# Revit family: Grab Rail_Metlam_Straight_Horizontal
name_source: partatom
category: Specialty Equipment
revit_build: Autodesk Revit 2016 (Build: 20170117_1200(x64)
units: mm (PartAtom-declared; Revit-internal decimal feet)

## family parameters
Always vertical = Yes
Cut with Voids When Loaded = No
OmniClass Number = 23.40.20.21.47
OmniClass Title = Bath Grab Bars
Part Type = Normal
Room Calculation Point = Yes
Round Connector Dimension = Use Diameter
Shared = No
Work Plane-Based = No

## types (10) — shared parameters
Depth = 90 mm  [stored 0.295276 ft]
Description = Straight Grab Rail
Height = 32 mm  [stored 0.104987 ft]
Manufacturer = Metlam
Manufacturer_Depth = 90 mm  [stored 0.295276 ft]
Manufacturer_Height = 78 mm  [stored 0.255906 ft]
Manufacturer_URL__Product Specific = http://www.metlam.com.au
Material_ANZRS = z_Metlam_Metal_Stainless Steel_Satin
Type Comments = Grab Rails
URL = http://www.metlam.com.au

## per-type parameters (varying)
| type | Length | Manufacturer_Length | Manufacturer_Spec Code | Model |
| 1532long x 90d x 32h (ML336SS) | 1532 mm  [stored 5.02625 ft] | 1500 mm  [stored 4.92126 ft] | ML336SS | ML336SS |
| 1232long x 90d x 32h (ML335SS) | 1232 mm  [stored 4.04199 ft] | 1200 mm | ML335SS | ML335SS |
| 1032long x 90d x 32h (ML334_1SS) | 1032 mm | 1000 mm  [stored 3.28084 ft] | ML334_1SS | ML334_1SS |
| 932long x 90d x 32h (ML333_1SS) | 932 mm | 900 mm  [stored 2.95276 ft] | ML333_1SS | ML333_1SS |
| 782long x 90d x 32h (ML332SS) | 782 mm | 750 mm  [stored 2.46063 ft] | ML332SS | ML332SS |
| 632long x 90d x 32h (ML331_1SS) | 632 mm | 600 mm | ML331_1SS | ML331_1SS |
| 482long x 90d x 32h (ML330_1SS) | 482 mm | 450 mm  [stored 1.47638 ft] | ML330_1SS | ML330_1SS |
| 432long x 90d x 32h (ML329SS) | 432 mm | 400 mm  [stored 1.31234 ft] | ML329SS | ML329SS |
| 382long x 90d x 32h (ML328SS) | 382 mm | 350 mm  [stored 1.14829 ft] | ML328SS | ML328SS |
| 332long x 90d x 32h (ML327_1SS) | 332 mm | 300 mm | ML327_1SS | ML327_1SS |

note: [stored X ft] marks values corroborated as IEEE doubles in the binary element streams (Revit-internal decimal feet)

## geometry (parser evidence)
native form markers: Sweep x2
no freeform markers — native parametric forms only
